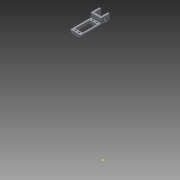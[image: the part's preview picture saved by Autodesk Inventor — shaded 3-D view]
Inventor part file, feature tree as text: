
AUTODESK INVENTOR PART (.ipt)
format: ipt  version: 2015 (Build 190159000, 159)  size: 166,912 bytes
history: native  units: in
note: dims shown in document units (in); Inventor stores cm internally (conversion verified against a paired STEP export)
features: reference x14, sketch x9, extrude x7, projected_geometry x3, plane x2, chamfer x1
ambient origin geometry x8: Origin, YZ Plane, XZ Plane, XY Plane, X Axis, Y Axis, Z Axis, Center Point
bodies: Solid1 (feature_tree)
feature tree (36):
  plane  "Work Plane1"
  plane  "Work Plane2"
  extrude  "Extrusion1"  Depth=2.4375in TaperAngle=0.0deg
  extrude  "Extrusion2"  Depth=0.75in TaperAngle=0.0deg
  extrude  "Extrusion3"  TaperAngle=180.0deg  [1 undecoded]
  extrude  "Extrusion4"  Depth=0.5in
  extrude  "Extrusion5"  Depth=0.5in TaperAngle=0.0deg
  extrude  "Extrusion6"  [1 undecoded]
  sketch  "Sketch10"
  extrude  "Extrusion7"  [1 undecoded]
  chamfer  "Chamfer1"  [1 undecoded]
  sketch  "Sketch12"
  sketch  "Sketch2"  dims[d0=2.4375in d1=0.0in d2=2.4375in d3=0.0in]
  reference  "Reference1"
  reference  "Reference2"
  sketch  "Sketch3"  dims[d4=2.4375in d5=0.0in d6=0.75in d7=0.0in]
  reference  "Reference3"
  reference  "Reference4"
  reference  "Reference5"
  reference  "Reference6"
  sketch  "Sketch4"  dims[d8=0.5625in d9=0.0in d10=180.0deg]
  reference  "Reference7"
  reference  "Reference8"
  reference  "Reference9"
  reference  "Reference10"
  sketch  "Sketch6"  dims[d11=0.5in d12=0.0in d13=0.1406in]
  projected_geometry  "Projected Loop1"
  sketch  "Sketch7"  dims[d14=0.1406in d15=0.5in d16=0.0in]
  reference  "Reference13"
  reference  "Reference14"
  reference  "Reference15"
  reference  "Reference16"
  sketch  "Sketch8"  dims[d17=0.1875in d18=0.125in d19=45.0deg]
  projected_geometry  "Projected Loop2"
  sketch  "Sketch11"
  projected_geometry  "Projected Loop3"
note: 4 required parameter values undecoded (feature->parameter linkage not recoverable at this tier; creation-order binding heuristic only, values carry confidence <= 0.55)
